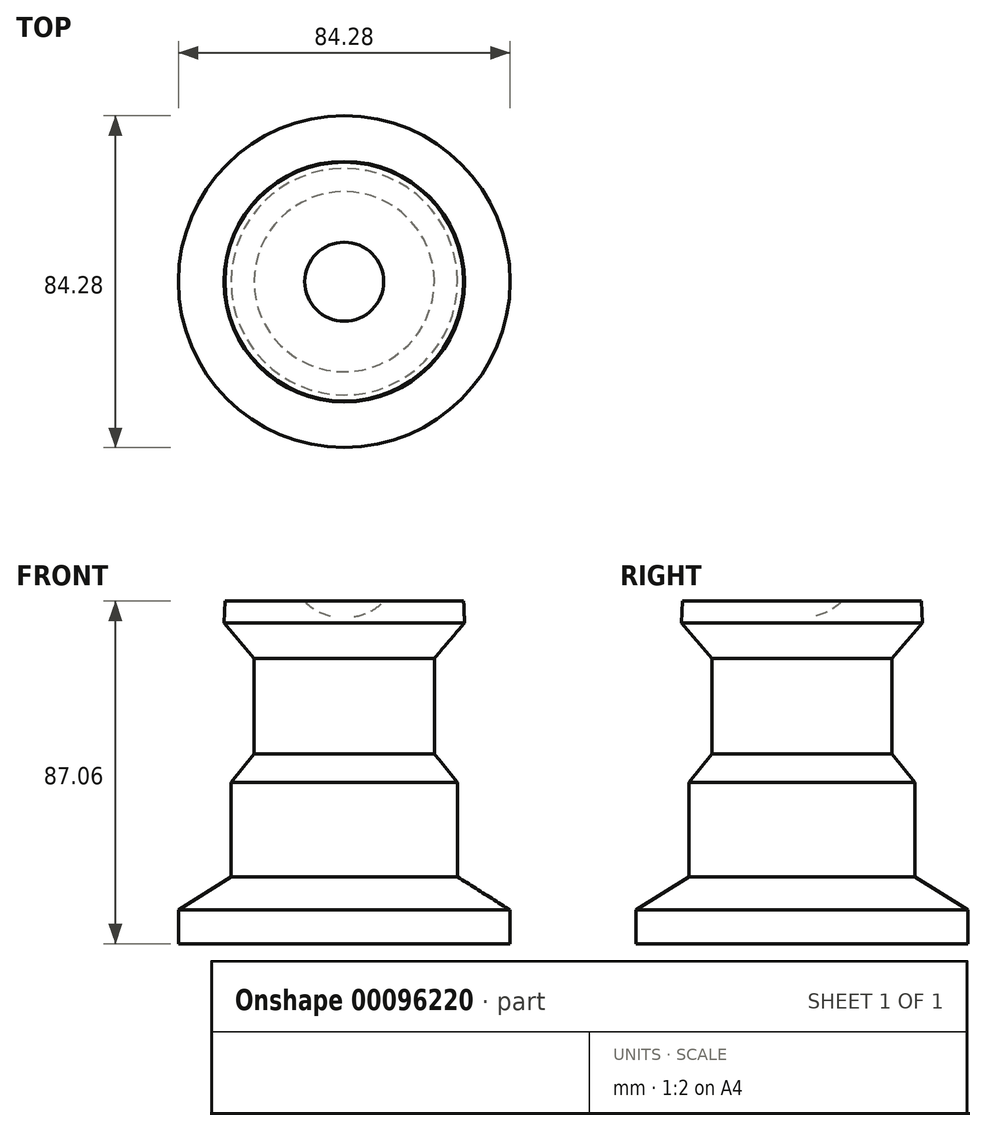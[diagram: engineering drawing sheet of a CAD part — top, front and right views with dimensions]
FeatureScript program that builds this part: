
annotation { "Feature Type Name" : "Feature", "Feature Type Description" : "" }
export const myFeature = defineFeature(function(context is Context, id is Id, definition is map)
    precondition{}
    {
        {
            var Q0;
            Q0=qCreatedBy(makeId("Front.planeOp"),FACE);
            var sketch = newSketch(context, id + "F0", { "sketchPlane" : qUnion([Q0])});
            skLineSegment(sketch, "E0", {"start": v(-28.77, -23.97) * mm, "end": v(-28.77, 0) * mm});
            skLineSegment(sketch, "E1", {"start": v(-28.77, 0) * mm, "end": v(-22.87, 7.25) * mm});
            skLineSegment(sketch, "E2", {"start": v(-22.87, 7.25) * mm, "end": v(-22.87, 31.52) * mm});
            skArc(sketch, "E3", {"start": v(0, 65.51) * mm, "mid": v(-11.67, 59.24) * mm, "end": v(-10.04, 46.1) * mm});
            skLineSegment(sketch, "E4", {"start": v(0, 65.51) * mm, "end": v(0, -40.96) * mm});
            skLineSegment(sketch, "E5", {"start": v(0, -40.96) * mm, "end": v(-42.14, -40.96) * mm});
            skLineSegment(sketch, "E6", {"start": v(-42.14, -40.96) * mm, "end": v(-42.14, -32.43) * mm});
            skLineSegment(sketch, "E7", {"start": v(-42.14, -32.43) * mm, "end": v(-28.77, -23.97) * mm});
            skLineSegment(sketch, "E8", {"start": v(-22.87, 31.52) * mm, "end": v(-30.56, 40.55) * mm});
            skLineSegment(sketch, "E9", {"start": v(-30.56, 40.55) * mm, "end": v(-30.33, 46.1) * mm});
            skLineSegment(sketch, "E10", {"start": v(-30.33, 46.1) * mm, "end": v(-10.04, 46.1) * mm});
            skSolve(sketch);
        }
        {
            var Q0;
            Q0 = qSketchRegion(id + "F0", true);
            var Q1;
            Q1=makeQuery(id+"F0.imprint","IMPRINT",FACE,{"disambiguationData":[TD([[makeQuery(id+"F0.imprint","IMPRINT",EDGE,{"derivedFrom":sQuery(id+"F0.wireOp",EDGE,"KTPjnBuz-9BAR-5Wjj-kbGL-r61XcjUnlZvw")}),-1.0]])]});
            var Q2;
            Q2=sQuery(id+"F0.wireOp",EDGE,"E4");
            revolve(context, id + "F1", {"entities" : qUnion([Q0, Q1]), "axis" : qUnion([Q2]), "revolveType" : RevolveType.FULL});
        }
    });
